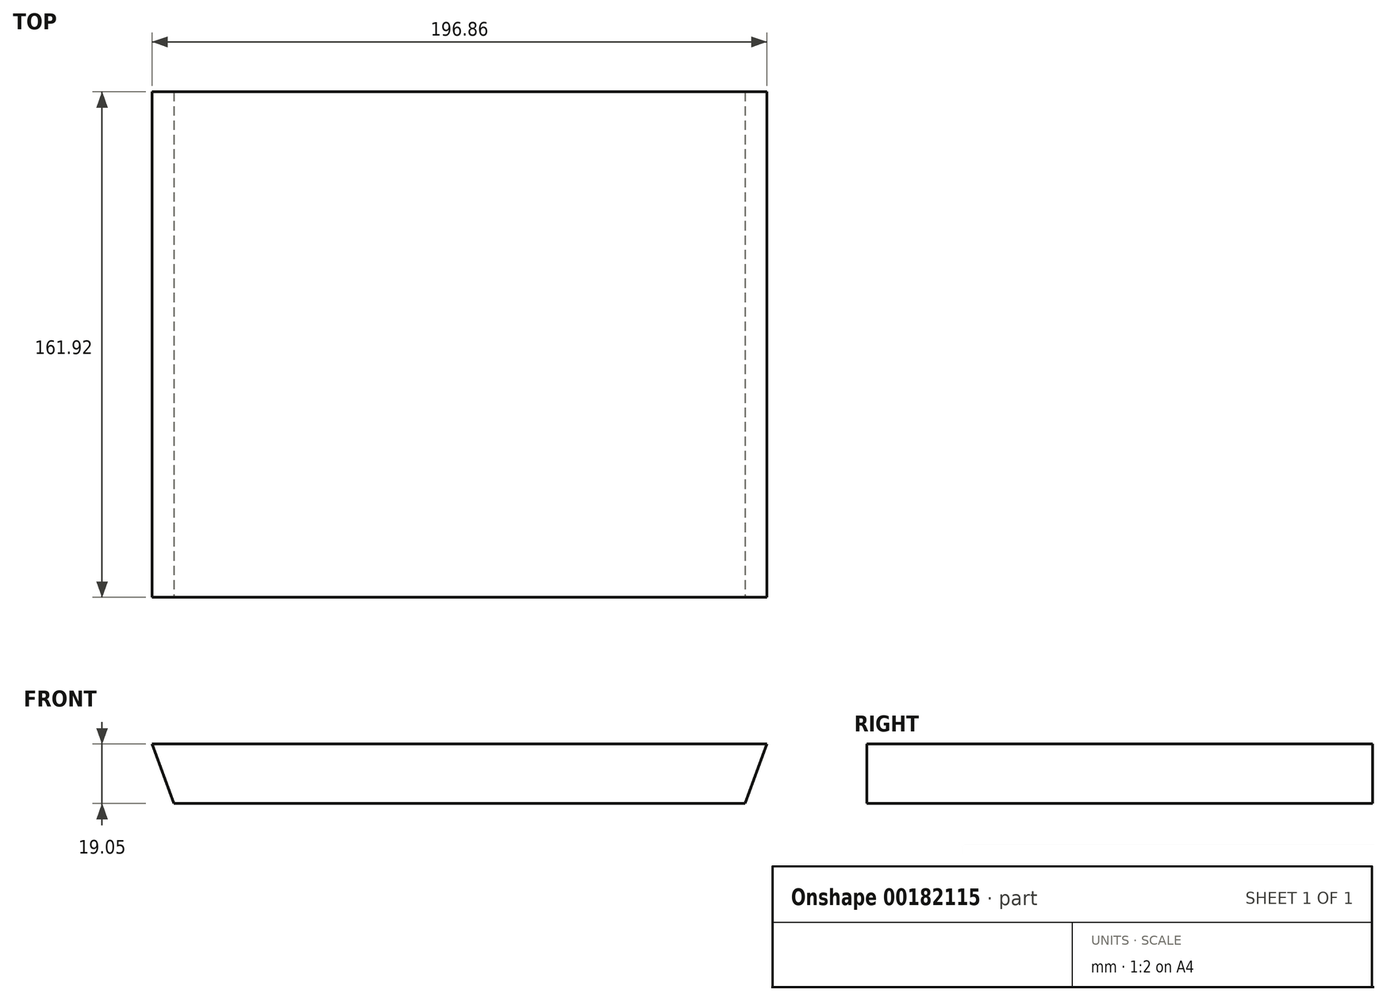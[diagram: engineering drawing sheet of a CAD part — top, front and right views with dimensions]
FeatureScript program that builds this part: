
annotation { "Feature Type Name" : "Feature", "Feature Type Description" : "" }
export const myFeature = defineFeature(function(context is Context, id is Id, definition is map)
    precondition{}
    {
        {
            var Q0;
            Q0=qCreatedBy(makeId("Top.planeOp"),FACE);
            var sketch = newSketch(context, id + "F0", { "sketchPlane" : qUnion([Q0])});
            skLineSegment(sketch, "E0.bottom", {"start": v(-98.43, 80.96) * mm, "end": v(98.43, 80.96) * mm});
            skLineSegment(sketch, "E0.top", {"start": v(-98.43, -80.96) * mm, "end": v(98.43, -80.96) * mm});
            skLineSegment(sketch, "E0.left", {"start": v(-98.42, 80.96) * mm, "end": v(-98.43, -80.96) * mm});
            skLineSegment(sketch, "E0.right", {"start": v(98.43, 80.96) * mm, "end": v(98.42, -80.96) * mm});
            skSolve(sketch);
        }
        {
            var Q0;
            Q0 = qSketchRegion(id + "F0", true);
            extrude(context, id + "F1", {"entities" : qUnion([Q0]), "depth" : 19.05 * mm});
        }
        {
            var Q0;
            Q0=makeQuery(id+"F1.opExtrude","SWEPT_FACE",FACE,{"disambiguationData":[OSD([sQuery(id+"F0.wireOp",EDGE,"E0.top")])]});
            var sketch = newSketch(context, id + "F2", { "sketchPlane" : qUnion([Q0])});
            skLineSegment(sketch, "E1", {"start": v(-98.43, 19.05) * mm, "end": v(-91.5, 0) * mm});
            skLineSegment(sketch, "E2", {"start": v(-91.5, 0) * mm, "end": v(91.5, 0) * mm});
            skLineSegment(sketch, "E3", {"start": v(91.5, 0) * mm, "end": v(98.43, 19.05) * mm});
            skLineSegment(sketch, "E4", {"start": v(98.43, 19.05) * mm, "end": v(98.43, -13.33) * mm});
            skLineSegment(sketch, "E5", {"start": v(98.43, -13.33) * mm, "end": v(-98.42, -13.33) * mm});
            skLineSegment(sketch, "E6", {"start": v(-98.42, -13.33) * mm, "end": v(-98.42, 19.05) * mm});
            skSolve(sketch);
        }
        {
            var Q0;
            Q0 = qSketchRegion(id + "F2", true);
            extrude(context, id + "F3", {"entities" : qUnion([Q0]), "operationType" : NewBodyOperationType.REMOVE, "endBound" : BoundingType.THROUGH_ALL, "oppositeDirection" : true, "depth" : 25.4 * mm});
        }
    });
